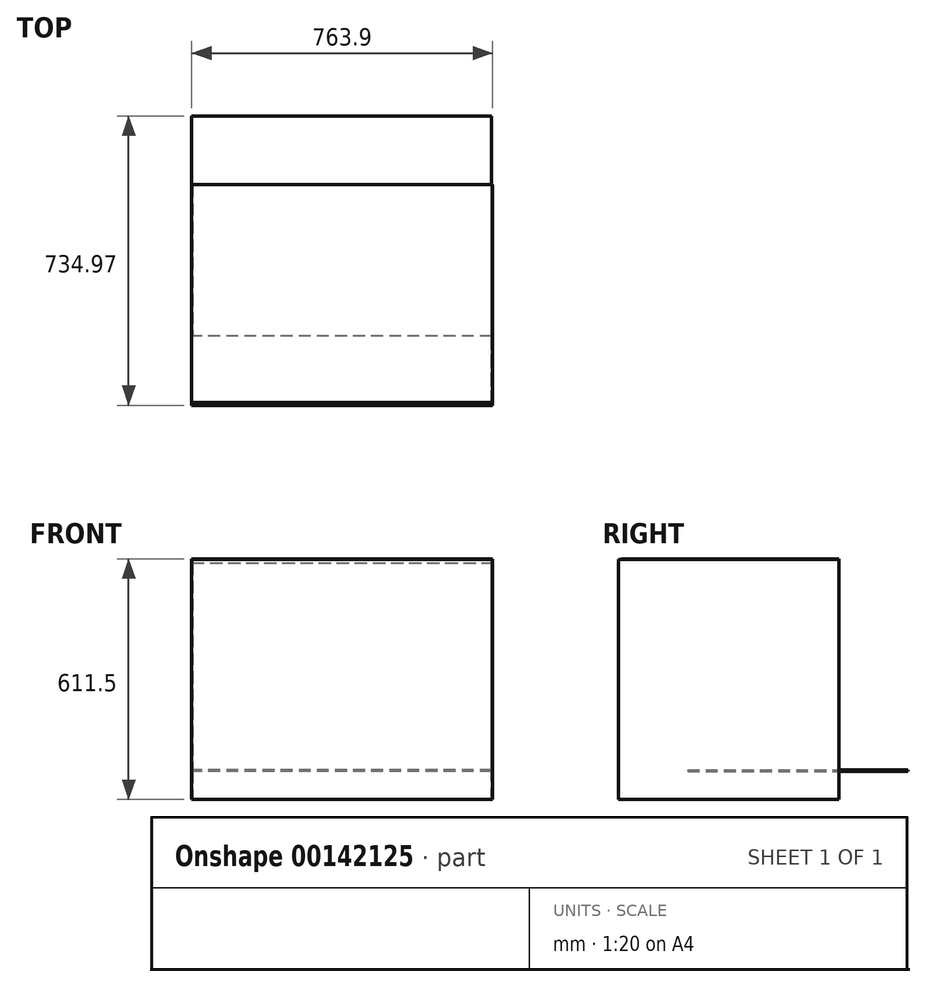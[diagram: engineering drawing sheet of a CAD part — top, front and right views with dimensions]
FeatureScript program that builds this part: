
annotation { "Feature Type Name" : "Feature", "Feature Type Description" : "" }
export const myFeature = defineFeature(function(context is Context, id is Id, definition is map)
    precondition{}
    {
        {
            var Q0;
            Q0=qCreatedBy(makeId("Top.planeOp"),FACE);
            var sketch = newSketch(context, id + "F0", { "sketchPlane" : qUnion([Q0])});
            skLineSegment(sketch, "E0.bottom", {"start": v(381, -279.4) * mm, "end": v(-381, -279.4) * mm});
            skLineSegment(sketch, "E0.top", {"start": v(381, 279.4) * mm, "end": v(-381, 279.4) * mm});
            skLineSegment(sketch, "E0.left", {"start": v(381, -279.4) * mm, "end": v(381, 279.4) * mm});
            skLineSegment(sketch, "E0.right", {"start": v(-381, -279.4) * mm, "end": v(-381, 279.4) * mm});
            skPoint(sketch, "E0.middle", {"position": v(0, 0) * mm});
            skSolve(sketch);
        }
        {
            var Q0;
            Q0 = qSketchRegion(id + "F0", true);
            extrude(context, id + "F1", {"entities" : qUnion([Q0]), "depth" : 3.04 * mm});
        }
        {
            var Q0;
            Q0=makeQuery(id+"F1.opExtrude","SWEPT_FACE",FACE,{"disambiguationData":[OSD([sQuery(id+"F0.wireOp",EDGE,"E0.left")])]});
            var sketch = newSketch(context, id + "F2", { "sketchPlane" : qUnion([Q0])});
            skLineSegment(sketch, "E1.bottom", {"start": v(-453.67, -71.82) * mm, "end": v(105.13, -71.82) * mm});
            skLineSegment(sketch, "E1.top", {"start": v(-453.67, 537.78) * mm, "end": v(105.13, 537.78) * mm});
            skLineSegment(sketch, "E1.left", {"start": v(-453.67, -71.82) * mm, "end": v(-453.67, 537.78) * mm});
            skLineSegment(sketch, "E1.right", {"start": v(105.13, -71.82) * mm, "end": v(105.13, 537.78) * mm});
            skSolve(sketch);
        }
        {
            var Q0;
            Q0 = qSketchRegion(id + "F2", true);
            extrude(context, id + "F3", {"entities" : qUnion([Q0]), "depth" : 1.9 * mm});
        }
        {
            var Q0;
            Q0=makeQuery(id+"F3.opExtrude","SWEPT_FACE",FACE,{"disambiguationData":[OSD([sQuery(id+"F2.wireOp",EDGE,"E1.left")])]});
            var sketch = newSketch(context, id + "F4", { "sketchPlane" : qUnion([Q0])});
            skLineSegment(sketch, "E2.bottom", {"start": v(382.9, -71.82) * mm, "end": v(-379.1, -71.82) * mm});
            skLineSegment(sketch, "E2.top", {"start": v(382.9, 537.78) * mm, "end": v(-379.1, 537.78) * mm});
            skLineSegment(sketch, "E2.left", {"start": v(382.9, -71.82) * mm, "end": v(382.9, 537.78) * mm});
            skLineSegment(sketch, "E2.right", {"start": v(-379.1, -71.82) * mm, "end": v(-379.1, 537.78) * mm});
            skSolve(sketch);
        }
        {
            var Q0;
            Q0 = qSketchRegion(id + "F4", true);
            extrude(context, id + "F5", {"entities" : qUnion([Q0]), "operationType" : NewBodyOperationType.ADD, "depth" : 1.9 * mm});
        }
        {
            var Q0;
            Q0=makeQuery(id+"F5.opExtrude","SWEPT_FACE",FACE,{"disambiguationData":[OSD([sQuery(id+"F4.wireOp",EDGE,"E2.right")])]});
            var sketch = newSketch(context, id + "F6", { "sketchPlane" : qUnion([Q0])});
            skLineSegment(sketch, "E3.bottom", {"start": v(455.57, 537.78) * mm, "end": v(-103.23, 537.78) * mm});
            skLineSegment(sketch, "E3.top", {"start": v(455.57, -71.82) * mm, "end": v(-103.23, -71.82) * mm});
            skLineSegment(sketch, "E3.left", {"start": v(455.57, 537.78) * mm, "end": v(455.57, -71.82) * mm});
            skLineSegment(sketch, "E3.right", {"start": v(-103.23, 537.78) * mm, "end": v(-103.23, -71.82) * mm});
            skSolve(sketch);
        }
        {
            var Q0;
            Q0 = qSketchRegion(id + "F6", true);
            extrude(context, id + "F7", {"entities" : qUnion([Q0]), "operationType" : NewBodyOperationType.ADD, "depth" : 1.9 * mm});
        }
        {
            var Q0;
            Q0=makeQuery(id+"F7.opExtrude","SWEPT_FACE",FACE,{"disambiguationData":[OSD([sQuery(id+"F6.wireOp",EDGE,"E3.right")])]});
            var sketch = newSketch(context, id + "F8", { "sketchPlane" : qUnion([Q0])});
            skLineSegment(sketch, "E4.bottom", {"start": v(381, -71.82) * mm, "end": v(-381, -71.82) * mm});
            skLineSegment(sketch, "E4.top", {"start": v(381, 529.52) * mm, "end": v(-381, 529.52) * mm});
            skLineSegment(sketch, "E4.left", {"start": v(381, -71.82) * mm, "end": v(381, 529.52) * mm});
            skLineSegment(sketch, "E4.right", {"start": v(-381, -71.82) * mm, "end": v(-381, 529.52) * mm});
            skSolve(sketch);
        }
        {
            var Q0;
            Q0 = qSketchRegion(id + "F8", true);
            extrude(context, id + "F9", {"entities" : qUnion([Q0]), "operationType" : NewBodyOperationType.ADD, "depth" : 1.9 * mm});
        }
        {
            var Q0;
            Q0=makeQuery(id+"F7.boolean.opBoolean","MERGE",FACE,{"derivedFrom":[makeQuery(id+"F5.boolean.opBoolean","MERGE",FACE,{"derivedFrom":[makeQuery(id+"F3.opExtrude","SWEPT_FACE",FACE,{"disambiguationData":[OSD([sQuery(id+"F2.wireOp",EDGE,"E1.top")])]}),makeQuery(id+"F5.opExtrude","SWEPT_FACE",FACE,{"disambiguationData":[OSD([sQuery(id+"F4.wireOp",EDGE,"E2.top")])]})]}),makeQuery(id+"F7.opExtrude","SWEPT_FACE",FACE,{"disambiguationData":[OSD([sQuery(id+"F6.wireOp",EDGE,"E3.bottom")])]})]});
            var sketch = newSketch(context, id + "F10", { "sketchPlane" : qUnion([Q0])});
            skLineSegment(sketch, "E5.bottom", {"start": v(-381, -447.83) * mm, "end": v(382.9, -447.83) * mm});
            skLineSegment(sketch, "E5.top", {"start": v(-381, 105.13) * mm, "end": v(382.9, 105.13) * mm});
            skLineSegment(sketch, "E5.left", {"start": v(-381, -455.57) * mm, "end": v(-381, 105.13) * mm});
            skLineSegment(sketch, "E5.right", {"start": v(382.9, -455.57) * mm, "end": v(382.9, 105.13) * mm});
            skSolve(sketch);
        }
        {
            var Q0;
            Q0 = qSketchRegion(id + "F10", true);
            extrude(context, id + "F11", {"entities" : qUnion([Q0]), "depth" : 1.9 * mm});
        }
    });
